# Revit family: TD92_PEK125_AZU070_RVT20_R00
name_source: partatom
category: Mobiliário
units: mm (PartAtom-declared; Revit-internal decimal feet)

## family parameters
Com base no plano de trabalho = Não
Compartilhado = Não
Corte com vazios quando carregada = Não
Número OmniClass = 23.40.20.00
Ponto de cálculo do ambiente = Não
Sempre na vertical = Sim
Título OmniClass = General Furniture and Specialties

## types (1)
- TD92_PEK125_AZU070_RVT20_R00
    Descrição = Para tornar a rotina das crianças ainda mais alegre e divertida, insira a Gangorra Infantil Tramontina Peek em Polietileno. Com um design muito especial e cor vibrante, ela vai compor perfeitamente o quarto ou o playground dos pequenos e transformar suas brincadeiras. Seu material é livre de toxinas e não prejudicial a saúdes. A escolha perfeita para compor o ambiente onde as crianças frequentam!
    Elevação padrão = 0  [stored 0 ft]
    Fabricante = Tramontina Delta S/A
    Modelo = Gangorra Infantil Tramontina Peek em Polietileno Azul
    Nota-chave = 92125070
    URL = https://www.tramontinastore.com

note: [stored X ft] marks values corroborated as IEEE doubles in the binary element streams (Revit-internal decimal feet)
